# Revit family: GD10 Tables
name_source: partatom
category: Furniture
revit_build: Autodesk Revit 2016 (Build: 20161004_0715(x64)
units: mm (PartAtom-declared; Revit-internal decimal feet)

## family parameters
Always vertical = Yes
Cut with Voids When Loaded = No
OmniClass Number = 23.40.20.00
OmniClass Title = General Furniture and Specialties
Room Calculation Point = No
Shared = No
Work Plane-Based = No

## types (10) — shared parameters
1100 High Bottom Rail = No
Assembly Code = E2020200
Frame = Gresham - SOLID OAK
Height = 742 mm  [stored 2.43438 ft]
Manufacturer = Gresham Office Furniture
Range = GD10
Table Top = Gresham - SOLID OAK
URL = www.gof.co.uk

## per-type parameters (varying)
| type | Central Cross Rail | Depth | Product Code | Width |
| 1600 x 900 x 742 | No | 900 mm  [stored 2.95276 ft] | GD10A1 | 1600 mm  [stored 5.24934 ft] |
| 1800 x 900 x 742 | No | 900 mm  [stored 2.95276 ft] | GD10A2 | 1800 mm  [stored 5.90551 ft] |
| 2000 x 900 x 742 | No | 900 mm  [stored 2.95276 ft] | GD10A3 | 2000 mm  [stored 6.56168 ft] |
| 2200 x 900 x 742 | Yes | 900 mm  [stored 2.95276 ft] | GD10A4 | 2200 mm |
| 2400 x 900 x 742 | Yes | 900 mm  [stored 2.95276 ft] | GD10A5 | 2400 mm |
| 1600 x 1200 x 742 | No | 1200 mm  [stored 3.93701 ft] | GD10B1 | 1600 mm  [stored 5.24934 ft] |
| 1800 x 1200 x 742 | No | 1200 mm  [stored 3.93701 ft] | GD10B2 | 1800 mm  [stored 5.90551 ft] |
| 2000 x 1200 x 742 | No | 1200 mm  [stored 3.93701 ft] | GD10B3 | 2000 mm  [stored 6.56168 ft] |
| 2200 x 1200 x 742 | Yes | 1200 mm  [stored 3.93701 ft] | GD10B4 | 2200 mm |
| 2400 x 1200 x 742 | Yes | 1200 mm  [stored 3.93701 ft] | GD10B5 | 2400 mm |

note: [stored X ft] marks values corroborated as IEEE doubles in the binary element streams (Revit-internal decimal feet)

## geometry (parser evidence)
native form markers: Sweep x4
no freeform markers — native parametric forms only
